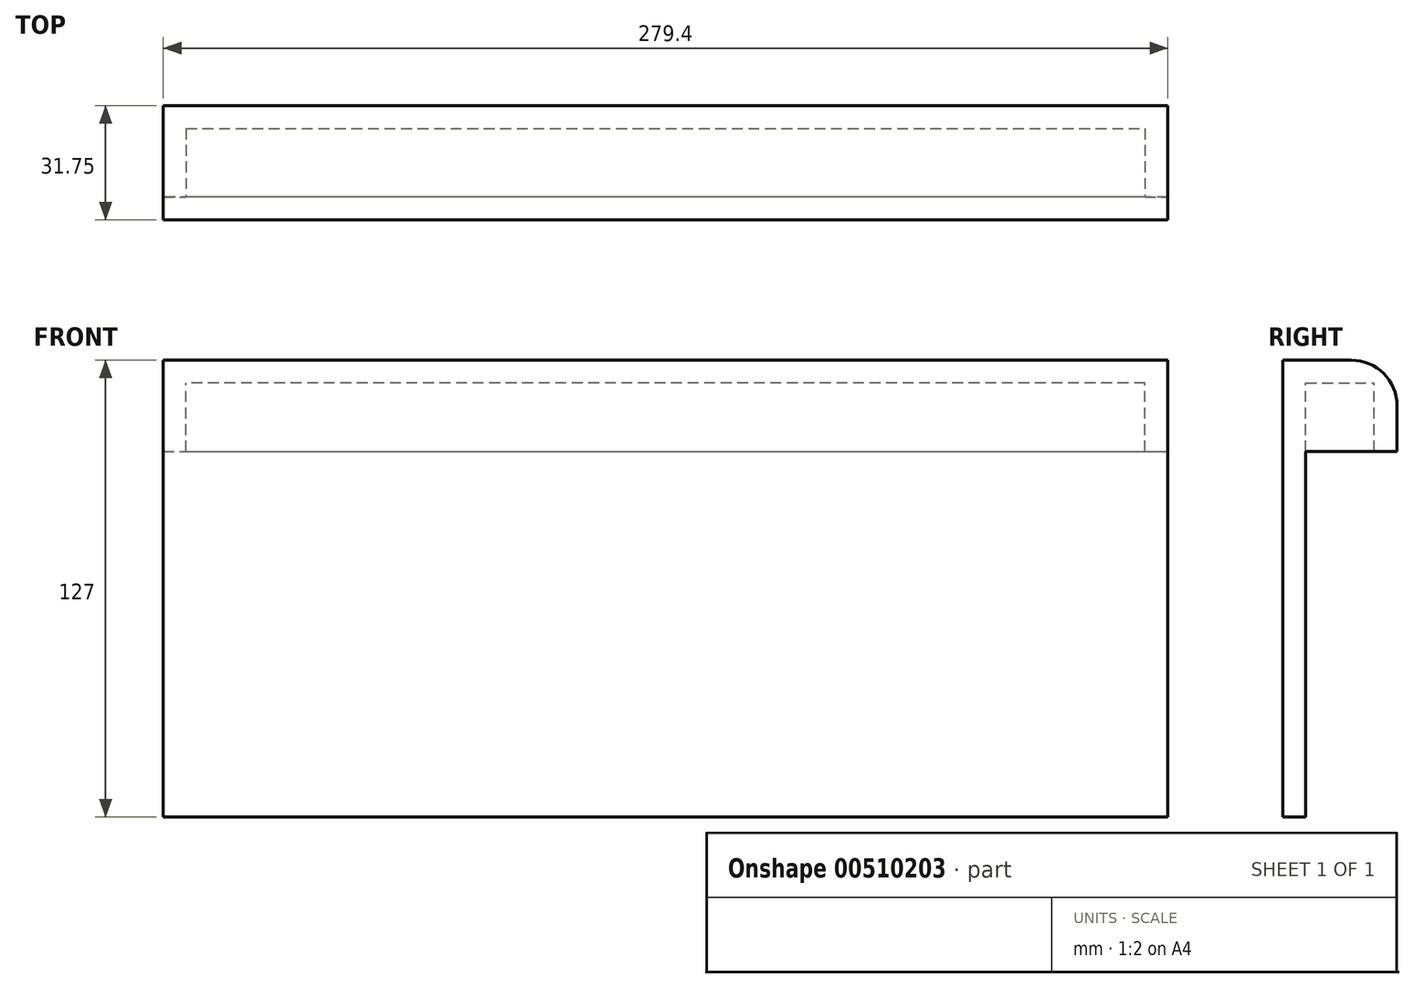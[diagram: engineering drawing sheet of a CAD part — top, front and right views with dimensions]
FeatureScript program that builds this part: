
annotation { "Feature Type Name" : "Feature", "Feature Type Description" : "" }
export const myFeature = defineFeature(function(context is Context, id is Id, definition is map)
    precondition{}
    {
        {
            var Q0;
            Q0=qCreatedBy(makeId("Front.planeOp"),FACE);
            var sketch = newSketch(context, id + "F0", { "sketchPlane" : qUnion([Q0])});
            skLineSegment(sketch, "E0.bottom", {"start": v(139.7, -63.5) * mm, "end": v(-139.7, -63.5) * mm});
            skLineSegment(sketch, "E0.top", {"start": v(139.7, 63.5) * mm, "end": v(-139.7, 63.5) * mm});
            skLineSegment(sketch, "E0.left", {"start": v(139.7, -63.5) * mm, "end": v(139.7, 63.5) * mm});
            skLineSegment(sketch, "E0.right", {"start": v(-139.7, -63.5) * mm, "end": v(-139.7, 63.5) * mm});
            skPoint(sketch, "E0.middle", {"position": v(0, 0) * mm});
            skPoint(sketch, "E1.endSnap0", {"position": v(0, 63.5) * mm});
            skLineSegment(sketch, "E2", {"start": v(-139.7, 38.1) * mm, "end": v(139.7, 38.1) * mm});
            skLineSegment(sketch, "E3", {"start": v(0, 50.8) * mm, "end": v(139.7, 50.8) * mm});
            skLineSegment(sketch, "E4", {"start": v(139.7, 50.8) * mm, "end": v(-139.7, 50.8) * mm});
            skSolve(sketch);
        }
        {
            var Q0;
            {var subQ0=sQuery(id+"F0.wireOp",EDGE,"E0.bottom");Q0=makeQuery(id+"F0.imprint","IMPRINT",FACE,{"disambiguationData":[TD([[makeQuery(id+"F0.imprint","IMPRINT",EDGE,{"derivedFrom":subQ0}),-1.0]])]});}
            var Q1;
            {var subQ4=sQuery(id+"F0.wireOp",EDGE,"E2");Q1=makeQuery(id+"F0.imprint","IMPRINT",FACE,{"disambiguationData":[TD([[makeQuery(id+"F0.imprint","IMPRINT",EDGE,{"derivedFrom":subQ4}),1.0]])]});}
            var Q2;
            {var subQ1=sQuery(id+"F0.wireOp",EDGE,"E0.top");Q2=makeQuery(id+"F0.imprint","IMPRINT",FACE,{"disambiguationData":[TD([[makeQuery(id+"F0.imprint","IMPRINT",EDGE,{"derivedFrom":subQ1}),1.0]])]});}
            extrude(context, id + "F1", {"entities" : qUnion([Q0, Q1, Q2]), "depth" : 6.35 * mm});
        }
        {
            var Q0;
            {var subQ1=sQuery(id+"F0.wireOp",EDGE,"E0.top");Q0=makeQuery(id+"F0.imprint","IMPRINT",FACE,{"disambiguationData":[TD([[makeQuery(id+"F0.imprint","IMPRINT",EDGE,{"derivedFrom":subQ1}),1.0]])]});}
            var Q1;
            {var subQ4=sQuery(id+"F0.wireOp",EDGE,"E2");Q1=makeQuery(id+"F0.imprint","IMPRINT",FACE,{"disambiguationData":[TD([[makeQuery(id+"F0.imprint","IMPRINT",EDGE,{"derivedFrom":subQ4}),1.0]])]});}
            extrude(context, id + "F2", {"entities" : qUnion([Q0, Q1]), "operationType" : NewBodyOperationType.ADD, "oppositeDirection" : true, "depth" : 25.4 * mm});
        }
        {
            var Q0;
            Q0=makeQuery(id+"F2.opExtrude","SWEPT_FACE",FACE,{"disambiguationData":[OSD([sQuery(id+"F0.wireOp",EDGE,"E2")])]});
            shell(context, id + "F3", {"entities" : qUnion([Q0]), "thickness" : 6.35 * mm});
        }
        {
            var Q0;
            Q0=makeQuery(id+"F2.opExtrude","CAP_EDGE",EDGE,{"disambiguationData":[OSD([sQuery(id+"F0.wireOp",EDGE,"E0.top")])],"isStart":false});
            fillet(context, id + "F4", {"entities" : qUnion([Q0]), "radius" : 12.7 * mm, "tangentPropagation" : true, "allowEdgeOverflow" : false});
        }
    });
